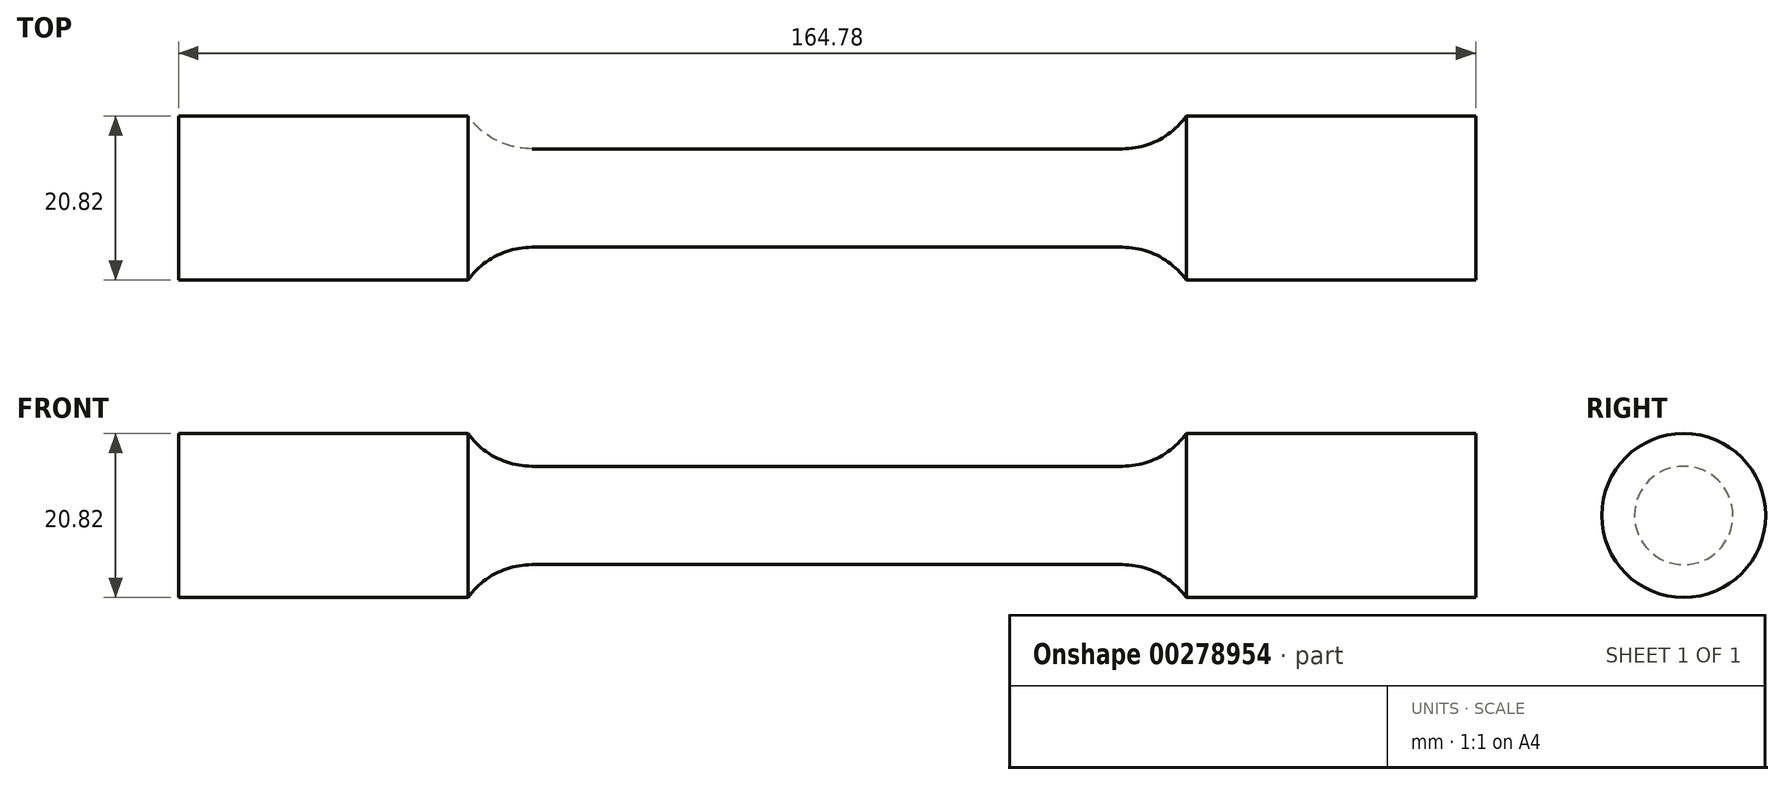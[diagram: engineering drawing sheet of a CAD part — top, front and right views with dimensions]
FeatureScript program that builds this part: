
annotation { "Feature Type Name" : "Feature", "Feature Type Description" : "" }
export const myFeature = defineFeature(function(context is Context, id is Id, definition is map)
    precondition{}
    {
        {
            var Q0;
            Q0=qCreatedBy(makeId("Front.planeOp"),FACE);
            var sketch = newSketch(context, id + "F0", { "sketchPlane" : qUnion([Q0])});
            skLineSegment(sketch, "E0", {"start": v(0, 6.25) * mm, "end": v(37.5, 6.25) * mm});
            skArc(sketch, "E1", {"start": v(37.5, 6.25) * mm, "mid": v(42.06, 7.35) * mm, "end": v(45.62, 10.41) * mm});
            skLineSegment(sketch, "E2", {"start": v(45.62, 10.41) * mm, "end": v(82.39, 10.41) * mm});
            skLineSegment(sketch, "E3", {"start": v(82.39, 10.41) * mm, "end": v(82.39, 0) * mm});
            skLineSegment(sketch, "E4.MirrorCS", {"start": v(0, 6.25) * mm, "end": v(-37.5, 6.25) * mm});
            skLineSegment(sketch, "E5.MirrorCS", {"start": v(-82.39, 10.41) * mm, "end": v(-82.39, 0) * mm});
            skLineSegment(sketch, "E6.MirrorCS", {"start": v(-45.62, 10.41) * mm, "end": v(-82.39, 10.41) * mm});
            skArc(sketch, "E7.MirrorCS", {"start": v(-37.5, 6.25) * mm, "mid": v(-42.06, 7.35) * mm, "end": v(-45.62, 10.41) * mm});
            skLineSegment(sketch, "E8", {"start": v(-82.39, 0) * mm, "end": v(82.39, 0) * mm});
            skSolve(sketch);
        }
        {
            var Q0;
            Q0=makeQuery(id+"F0.imprint","IMPRINT",FACE,{"disambiguationData":[TD([[makeQuery(id+"F0.imprint","IMPRINT",EDGE,{"derivedFrom":sQuery(id+"F0.wireOp",EDGE,"E0")}),-1.0]])]});
            var Q1;
            Q1=sQuery(id+"F0.wireOp",EDGE,"E8");
            revolve(context, id + "F1", {"entities" : qUnion([Q0]), "axis" : qUnion([Q1]), "revolveType" : RevolveType.FULL});
        }
    });
